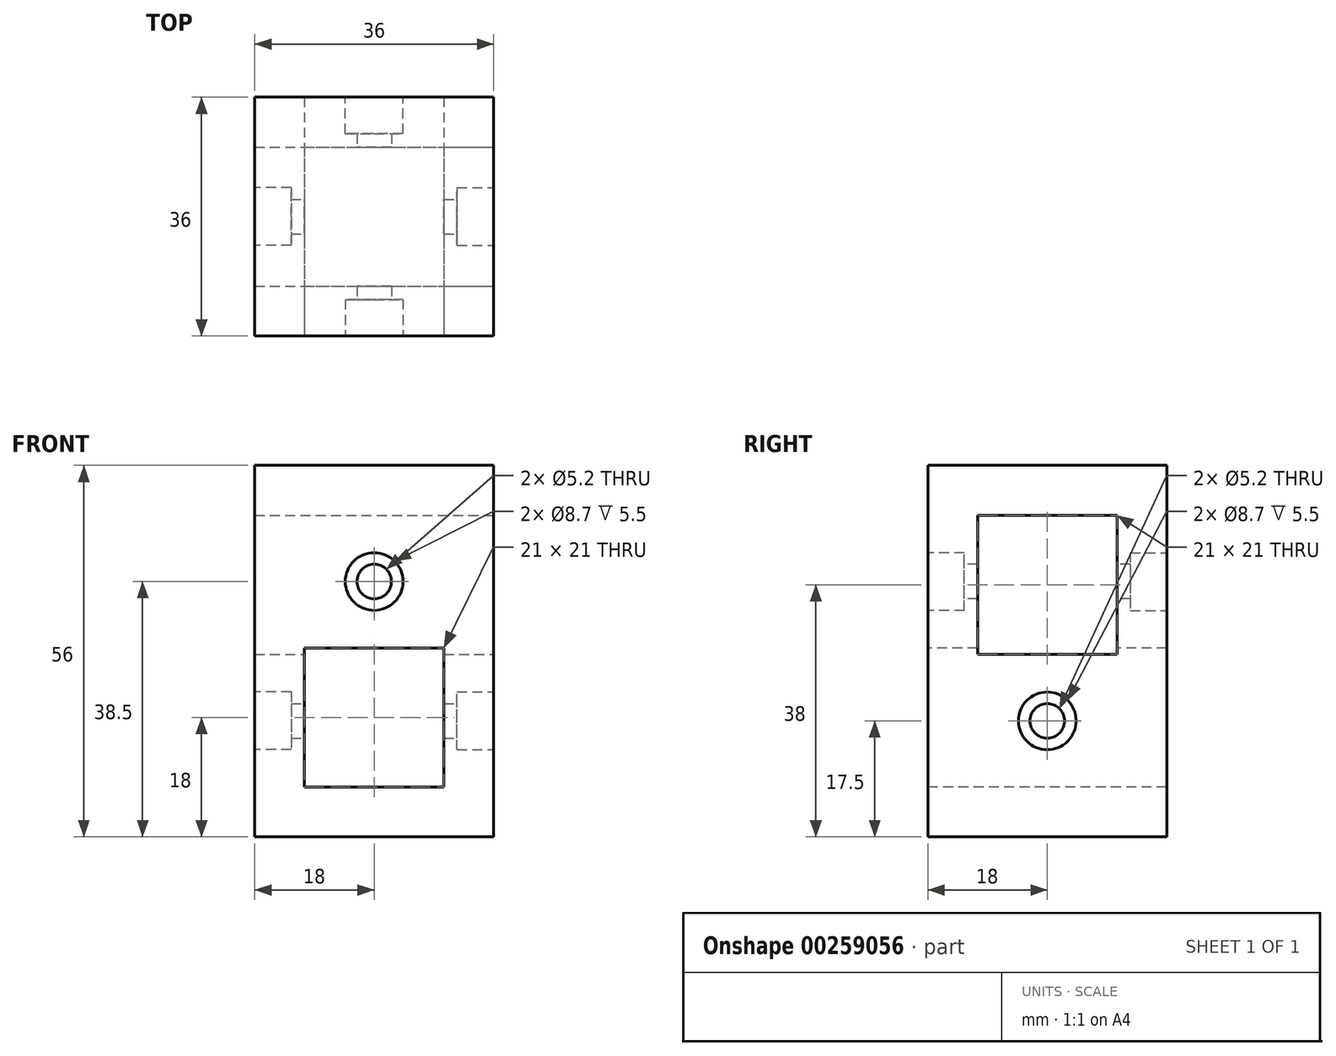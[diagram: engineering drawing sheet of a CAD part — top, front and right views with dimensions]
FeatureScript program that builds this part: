
annotation { "Feature Type Name" : "Feature", "Feature Type Description" : "" }
export const myFeature = defineFeature(function(context is Context, id is Id, definition is map)
    precondition{}
    {
        {
            var Q0;
            Q0=qCreatedBy(makeId("Top.planeOp"),FACE);
            var sketch = newSketch(context, id + "F0", { "sketchPlane" : qUnion([Q0])});
            skLineSegment(sketch, "E0.bottom", {"start": v(0, 36) * mm, "end": v(36, 36) * mm});
            skLineSegment(sketch, "E0.top", {"start": v(0, 0) * mm, "end": v(36, 0) * mm});
            skLineSegment(sketch, "E0.left", {"start": v(0, 36) * mm, "end": v(0, 0) * mm});
            skLineSegment(sketch, "E0.right", {"start": v(36, 36) * mm, "end": v(36, 0) * mm});
            skSolve(sketch);
        }
        {
            var Q0;
            Q0=makeQuery(id+"F0.imprint","IMPRINT",FACE,{"disambiguationData":[TD([[makeQuery(id+"F0.imprint","IMPRINT",EDGE,{"derivedFrom":sQuery(id+"F0.wireOp",EDGE,"E0.bottom")}),-1.0]])]});
            extrude(context, id + "F1", {"entities" : qUnion([Q0]), "depth" : 56 * mm});
        }
        {
            var Q0;
            Q0=makeQuery(id+"F1.opExtrude","SWEPT_FACE",FACE,{"disambiguationData":[OSD([sQuery(id+"F0.wireOp",EDGE,"E0.top")])]});
            var sketch = newSketch(context, id + "F2", { "sketchPlane" : qUnion([Q0])});
            skLineSegment(sketch, "E1.bottom", {"start": v(28.5, 7.5) * mm, "end": v(7.5, 7.5) * mm});
            skLineSegment(sketch, "E1.top", {"start": v(28.5, 28.5) * mm, "end": v(7.5, 28.5) * mm});
            skLineSegment(sketch, "E1.left", {"start": v(28.5, 7.5) * mm, "end": v(28.5, 28.5) * mm});
            skLineSegment(sketch, "E1.right", {"start": v(7.5, 7.5) * mm, "end": v(7.5, 28.5) * mm});
            skCircle(sketch, "E2", {"center": v(18, 38.5) * mm, "radius": 2.6 * mm});
            skSolve(sketch);
        }
        {
            var Q0;
            Q0 = qSketchRegion(id + "F2", true);
            extrude(context, id + "F3", {"entities" : qUnion([Q0]), "operationType" : NewBodyOperationType.REMOVE, "oppositeDirection" : true, "depth" : 50 * mm});
        }
        {
            var Q0;
            Q0=makeQuery(id+"F1.opExtrude","SWEPT_FACE",FACE,{"disambiguationData":[OSD([sQuery(id+"F0.wireOp",EDGE,"E0.right")])]});
            var sketch = newSketch(context, id + "F4", { "sketchPlane" : qUnion([Q0])});
            skLineSegment(sketch, "E3.bottom", {"start": v(28.5, 48.5) * mm, "end": v(7.5, 48.5) * mm});
            skLineSegment(sketch, "E3.top", {"start": v(28.5, 27.5) * mm, "end": v(7.5, 27.5) * mm});
            skLineSegment(sketch, "E3.left", {"start": v(28.5, 48.5) * mm, "end": v(28.5, 27.5) * mm});
            skLineSegment(sketch, "E3.right", {"start": v(7.5, 48.5) * mm, "end": v(7.5, 27.5) * mm});
            skCircle(sketch, "E4", {"center": v(18, 17.5) * mm, "radius": 2.6 * mm});
            skSolve(sketch);
        }
        {
            var Q0;
            Q0 = qSketchRegion(id + "F4", true);
            extrude(context, id + "F5", {"entities" : qUnion([Q0]), "operationType" : NewBodyOperationType.REMOVE, "oppositeDirection" : true, "depth" : 50 * mm});
        }
        {
            var Q0;
            Q0=makeQuery(id+"F1.opExtrude","SWEPT_FACE",FACE,{"disambiguationData":[OSD([sQuery(id+"F0.wireOp",EDGE,"E0.right")])]});
            var sketch = newSketch(context, id + "F6", { "sketchPlane" : qUnion([Q0])});
            skCircle(sketch, "E5", {"center": v(18, 17.5) * mm, "radius": 4.35 * mm});
            skSolve(sketch);
        }
        {
            var Q0;
            Q0 = qSketchRegion(id + "F6", true);
            extrude(context, id + "F7", {"entities" : qUnion([Q0]), "operationType" : NewBodyOperationType.REMOVE, "oppositeDirection" : true, "depth" : 5.5 * mm});
        }
        {
            var Q0;
            Q0=makeQuery(id+"F1.opExtrude","SWEPT_FACE",FACE,{"disambiguationData":[OSD([sQuery(id+"F0.wireOp",EDGE,"E0.left")])]});
            var sketch = newSketch(context, id + "F8", { "sketchPlane" : qUnion([Q0])});
            skCircle(sketch, "E6", {"center": v(-18, 17.5) * mm, "radius": 4.35 * mm});
            skSolve(sketch);
        }
        {
            var Q0;
            Q0 = qSketchRegion(id + "F8", true);
            extrude(context, id + "F9", {"entities" : qUnion([Q0]), "operationType" : NewBodyOperationType.REMOVE, "oppositeDirection" : true, "depth" : 5.5 * mm});
        }
        {
            var Q0;
            Q0=makeQuery(id+"F1.opExtrude","SWEPT_FACE",FACE,{"disambiguationData":[OSD([sQuery(id+"F0.wireOp",EDGE,"E0.bottom")])]});
            var sketch = newSketch(context, id + "F10", { "sketchPlane" : qUnion([Q0])});
            skCircle(sketch, "E7", {"center": v(-18, 38.5) * mm, "radius": 4.35 * mm});
            skSolve(sketch);
        }
        {
            var Q0;
            Q0 = qSketchRegion(id + "F10", true);
            extrude(context, id + "F11", {"entities" : qUnion([Q0]), "operationType" : NewBodyOperationType.REMOVE, "oppositeDirection" : true, "depth" : 5.5 * mm});
        }
        {
            var Q0;
            Q0=makeQuery(id+"F1.opExtrude","SWEPT_FACE",FACE,{"disambiguationData":[OSD([sQuery(id+"F0.wireOp",EDGE,"E0.top")])]});
            var sketch = newSketch(context, id + "F12", { "sketchPlane" : qUnion([Q0])});
            skCircle(sketch, "E8", {"center": v(18, 38.5) * mm, "radius": 4.35 * mm});
            skSolve(sketch);
        }
        {
            var Q0;
            Q0 = qSketchRegion(id + "F12", true);
            extrude(context, id + "F13", {"entities" : qUnion([Q0]), "operationType" : NewBodyOperationType.REMOVE, "oppositeDirection" : true, "depth" : 5.5 * mm});
        }
    });
